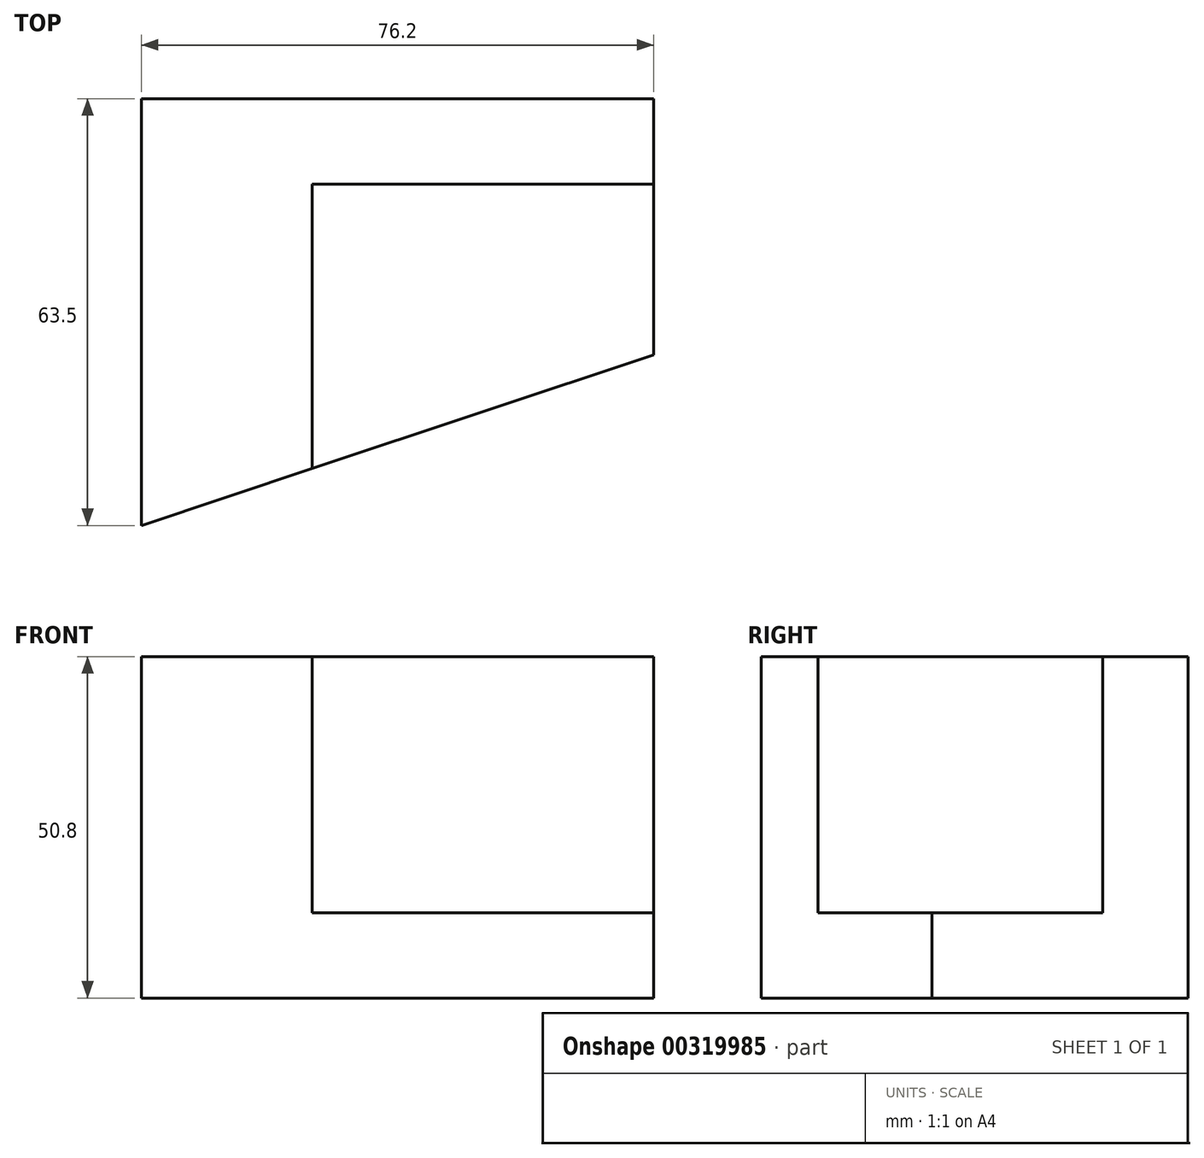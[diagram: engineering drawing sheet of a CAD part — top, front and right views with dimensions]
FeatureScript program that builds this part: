
annotation { "Feature Type Name" : "Feature", "Feature Type Description" : "" }
export const myFeature = defineFeature(function(context is Context, id is Id, definition is map)
    precondition{}
    {
        {
            var Q0;
            Q0=qCreatedBy(makeId("Front.planeOp"),FACE);
            var sketch = newSketch(context, id + "F0", { "sketchPlane" : qUnion([Q0])});
            skLineSegment(sketch, "E0", {"start": v(0, 0) * mm, "end": v(0, 50.8) * mm});
            skLineSegment(sketch, "E1", {"start": v(0, 50.8) * mm, "end": v(25.4, 50.8) * mm});
            skLineSegment(sketch, "E2", {"start": v(25.4, 50.8) * mm, "end": v(25.4, 12.7) * mm});
            skLineSegment(sketch, "E3", {"start": v(25.4, 12.7) * mm, "end": v(76.2, 12.7) * mm});
            skLineSegment(sketch, "E4", {"start": v(76.2, 12.7) * mm, "end": v(76.2, 0) * mm});
            skLineSegment(sketch, "E5", {"start": v(76.2, 0) * mm, "end": v(0, 0) * mm});
            skLineSegment(sketch, "E6", {"start": v(25.4, 50.8) * mm, "end": v(76.2, 50.8) * mm});
            skLineSegment(sketch, "E7", {"start": v(76.2, 50.8) * mm, "end": v(76.2, 12.7) * mm});
            skSolve(sketch);
        }
        {
            var Q0;
            Q0=makeQuery(id+"F0.imprint","IMPRINT",FACE,{"disambiguationData":[TD([[makeQuery(id+"F0.imprint","IMPRINT",EDGE,{"derivedFrom":sQuery(id+"F0.wireOp",EDGE,"E0")}),-1.0]])]});
            var Q1;
            Q1=makeQuery(id+"F0.imprint","IMPRINT",FACE,{"disambiguationData":[TD([[makeQuery(id+"F0.imprint","IMPRINT",EDGE,{"derivedFrom":sQuery(id+"F0.wireOp",EDGE,"E2")}),1.0]])]});
            extrude(context, id + "F1", {"entities" : qUnion([Q0, Q1]), "oppositeDirection" : true, "depth" : 63.5 * mm});
        }
        {
            var Q0;
            Q0=makeQuery(id+"F1.opExtrude","SWEPT_FACE",FACE,{"disambiguationData":[OSD([sQuery(id+"F0.wireOp",EDGE,"E1"),sQuery(id+"F0.wireOp",EDGE,"E6")])]});
            var sketch = newSketch(context, id + "F2", { "sketchPlane" : qUnion([Q0])});
            skLineSegment(sketch, "E8", {"start": v(0, 0) * mm, "end": v(76.2, 25.4) * mm});
            skSolve(sketch);
        }
        {
            var Q0;
            {var subQ0=sQuery(id+"F2.wireOp",EDGE,"E8");Q0=makeQuery(id+"F2.imprint","IMPRINT",FACE,{"disambiguationData":[TD([[makeQuery(id+"F2.imprint","IMPRINT",EDGE,{"derivedFrom":subQ0}),-1.0]])]});}
            extrude(context, id + "F3", {"entities" : qUnion([Q0]), "operationType" : NewBodyOperationType.REMOVE, "endBound" : BoundingType.THROUGH_ALL, "oppositeDirection" : true, "depth" : 25.4 * mm});
        }
        {
            var Q0;
            Q0=makeQuery(id+"F1.opExtrude","SWEPT_FACE",FACE,{"disambiguationData":[OSD([sQuery(id+"F0.wireOp",EDGE,"E1"),sQuery(id+"F0.wireOp",EDGE,"E6")])]});
            var sketch = newSketch(context, id + "F4", { "sketchPlane" : qUnion([Q0])});
            skLineSegment(sketch, "E9", {"start": v(25.4, 8.47) * mm, "end": v(25.4, 50.8) * mm});
            skLineSegment(sketch, "E10", {"start": v(25.4, 50.8) * mm, "end": v(76.2, 50.8) * mm});
            skSolve(sketch);
        }
        {
            var Q0;
            {var subQ0=sQuery(id+"F4.wireOp",EDGE,"E9");Q0=makeQuery(id+"F4.imprint","IMPRINT",FACE,{"disambiguationData":[TD([[makeQuery(id+"F4.imprint","IMPRINT",EDGE,{"derivedFrom":subQ0}),-1.0]])]});}
            extrude(context, id + "F5", {"entities" : qUnion([Q0]), "operationType" : NewBodyOperationType.REMOVE, "oppositeDirection" : true, "depth" : 38.1 * mm});
        }
    });
